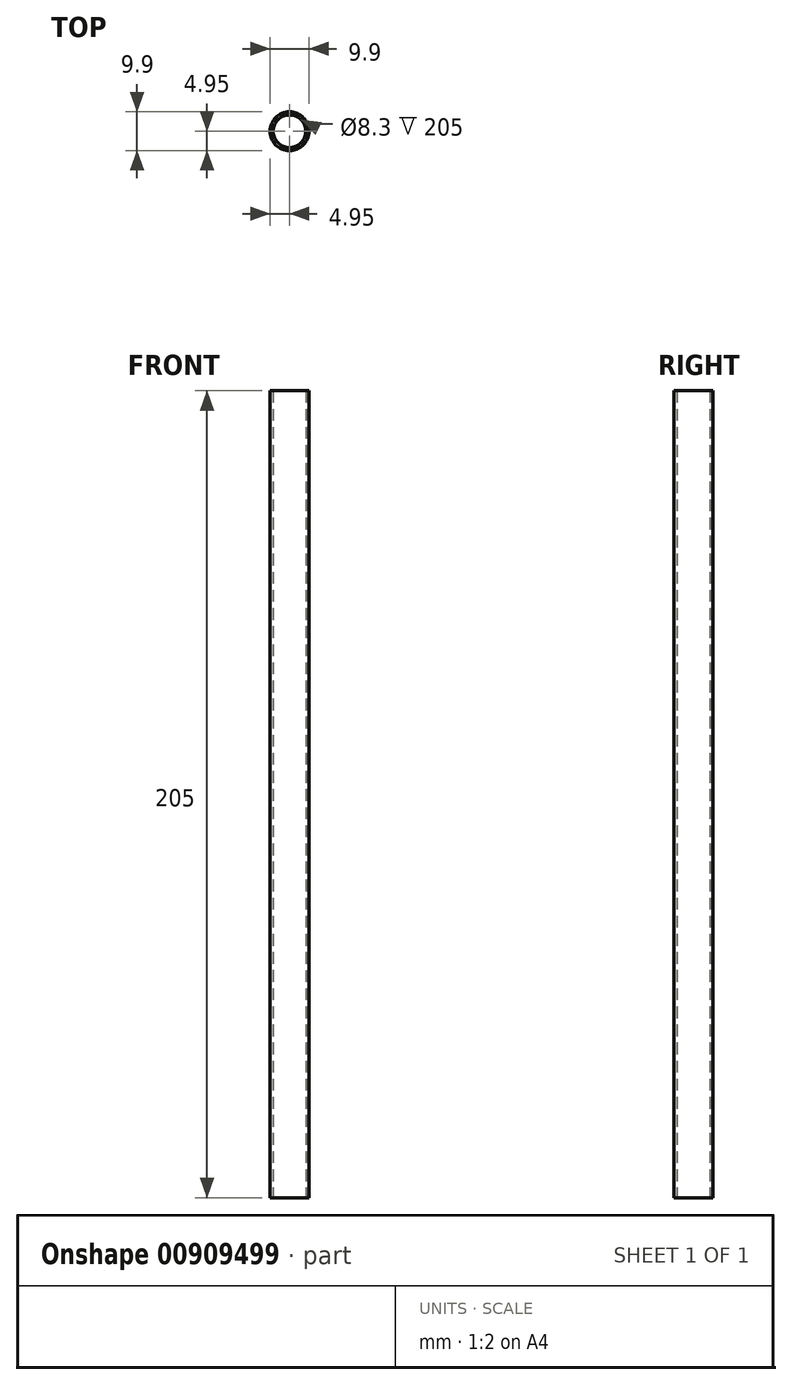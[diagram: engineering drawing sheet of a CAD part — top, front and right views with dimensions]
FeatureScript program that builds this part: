
annotation { "Feature Type Name" : "Feature", "Feature Type Description" : "" }
export const myFeature = defineFeature(function(context is Context, id is Id, definition is map)
    precondition{}
    {
        {
            var Q0;
            Q0=qCreatedBy(makeId("Top.planeOp"),FACE);
            var sketch = newSketch(context, id + "F0", { "sketchPlane" : qUnion([Q0])});
            skCircle(sketch, "E0", {"center": v(0, 0) * mm, "radius": 4.15 * mm});
            skCircle(sketch, "E1.0", {"center": v(0, 0) * mm, "radius": 4.95 * mm});
            skSolve(sketch);
        }
        {
            var Q0;
            Q0=makeQuery(id+"F0.imprint","IMPRINT",FACE,{"disambiguationData":[TD([[makeQuery(id+"F0.imprint","IMPRINT",EDGE,{"derivedFrom":sQuery(id+"F0.wireOp",EDGE,"E0")}),-1.0]])]});
            extrude(context, id + "F1", {"entities" : qUnion([Q0]), "depth" : 205 * mm, "offsetDistance" : 25 * mm});
        }
    });
